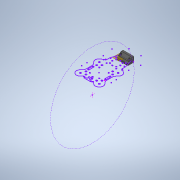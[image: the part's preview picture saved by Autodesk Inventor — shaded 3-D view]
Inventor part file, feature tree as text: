
AUTODESK INVENTOR PART (.ipt)
format: ipt  version: 2020 (Build 240168000, 168)  size: 567,296 bytes
history: native  units: in
note: dims shown in document units (in); Inventor stores cm internally (conversion verified against a paired STEP export)
features: sketch x11, extrude x10, plane x6, fillet x5, projected_geometry x5
ambient origin geometry x8: Origin, YZ Plane, XZ Plane, XY Plane, X Axis, Y Axis, Z Axis, Center Point
bodies: Solid2 (feature_tree)
feature tree (37):
  plane  "Work Plane1"
  plane  "Work Plane7"
  plane  "Work Plane4"
  plane  "Work Plane9"
  sketch  "Sketch13"  dims[d22=0.1181in d23=0.0in d24=0.2008in]
  plane  "Work Plane11"
  extrude  "Extrusion10"  Depth=0.1181in
  plane  "Work Plane8"
  sketch  "Sketch15"  dims[d35=0.0001in d36=1.378in d37=0.0in]
  extrude  "Extrusion12"  Depth=1.378in TaperAngle=0.0deg
  extrude  "Extrusion13"  Depth=1.378in TaperAngle=0.0deg
  extrude  "Extrusion14"  Depth=0.2244in
  extrude  "Extrusion15"  Depth=1.378in TaperAngle=0.0deg
  sketch  "Sketch20"  dims[d47=0.1181in d48=0.1181in d49=0.0in]
  extrude  "Extrusion16"  Depth=0.1181in
  extrude  "Extrusion17"  Depth=0.1181in TaperAngle=0.0deg
  extrude  "Extrusion18"  Depth=0.0394in TaperAngle=0.0deg
  extrude  "Extrusion19"  Depth=0.0394in
  fillet  "Fillet1"  Radius=0.1181in
  fillet  "Fillet2"  Radius=0.0394in
  fillet  "Fillet3"  Radius=0.0394in
  fillet  "Fillet4"  Radius=0.0118in
  fillet  "Fillet5"  Radius=0.0394in
  extrude  "Extrusion20"  Depth=1.9685in
  sketch  "Sketch14"  dims[d25=0.2008in d32=1.378in d33=0.0in]
  sketch  "Sketch17"  dims[d38=0.0in d39=0.0in d40=0.2244in]
  sketch  "Sketch18"  dims[d41=0.2244in d42=1.378in d43=0.0in]
  projected_geometry  "Projected Loop7"
  projected_geometry  "Projected Loop8"
  sketch  "Sketch19"  dims[d44=0.1181in d45=0.0in d46=0.1181in]
  sketch  "Sketch21"  dims[d50=0.0394in d51=0.0in d52=0.0394in d53=0.0in]
  sketch  "Sketch22"  dims[d54=0.1969in d55=0.0295in d56=0.1181in d57=0.0394in d58=0.0394in d60=0.0118in d61=0.0394in d62=0.0in]
  projected_geometry  "Projected Loop9"
  sketch  "Sketch23"  dims[d2=0.0197in d3=1.9685in]
  projected_geometry  "Projected Loop10"
  projected_geometry  "Projected Loop11"
  sketch  "Sketch24"  dims[d4=0.0197in d5=1.9685in d11=0.0197in d12=1.9685in d13=0.0197in d14=1.9685in d34=0.0197in]
